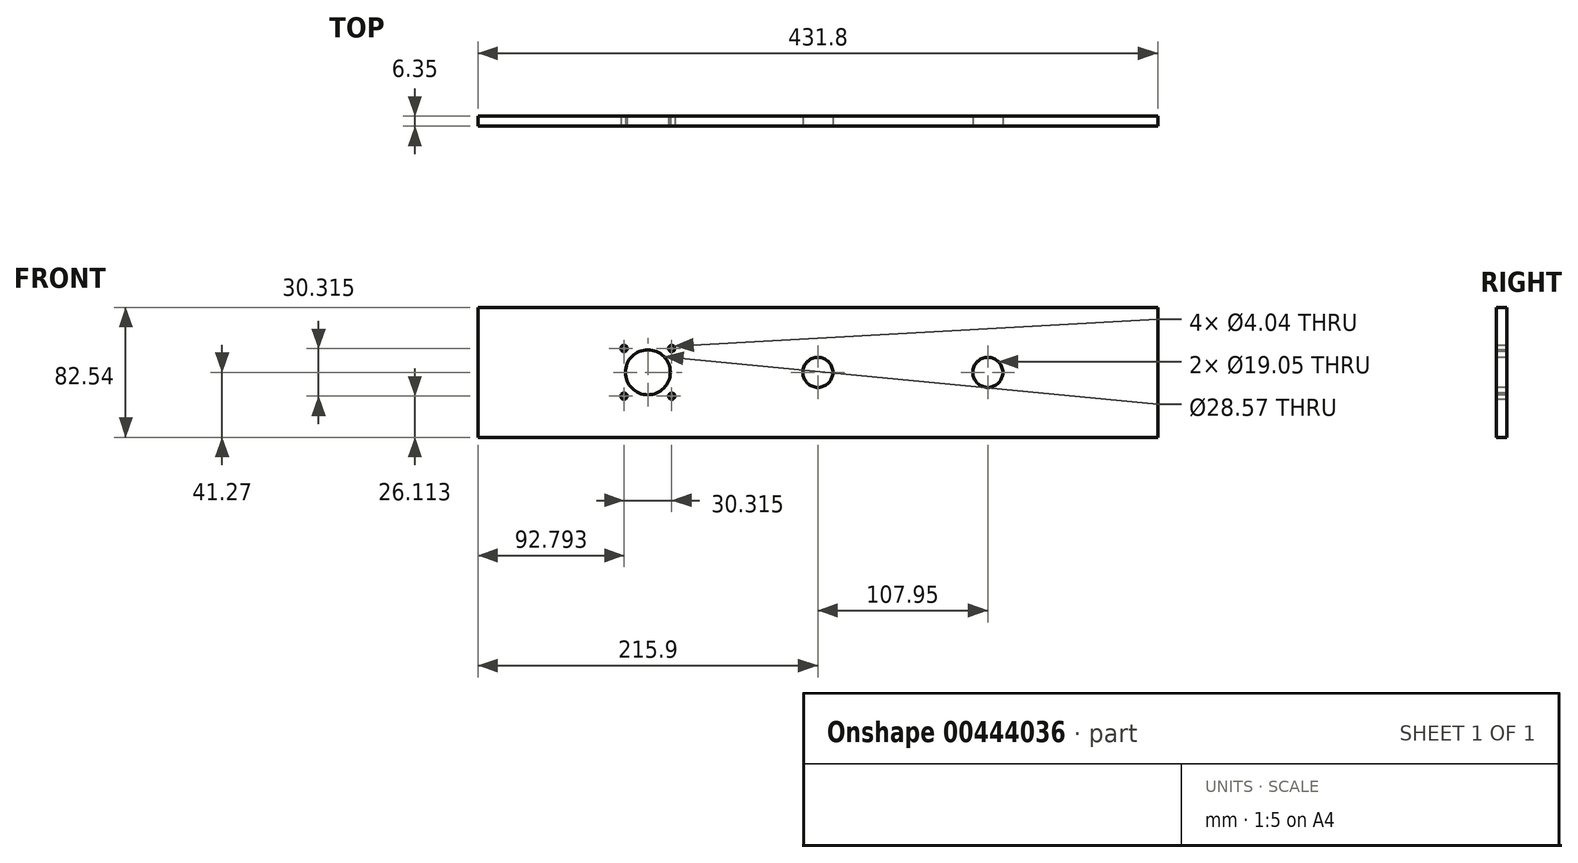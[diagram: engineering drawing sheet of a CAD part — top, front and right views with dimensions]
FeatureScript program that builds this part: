
annotation { "Feature Type Name" : "Feature", "Feature Type Description" : "" }
export const myFeature = defineFeature(function(context is Context, id is Id, definition is map)
    precondition{}
    {
        {
            var Q0;
            Q0=qCreatedBy(makeId("Front.planeOp"),FACE);
            var sketch = newSketch(context, id + "F0", { "sketchPlane" : qUnion([Q0])});
            skLineSegment(sketch, "E0.bottom", {"start": v(215.9, 41.28) * mm, "end": v(-215.9, 41.28) * mm});
            skLineSegment(sketch, "E0.top", {"start": v(215.9, -41.28) * mm, "end": v(-215.9, -41.28) * mm});
            skLineSegment(sketch, "E0.left", {"start": v(215.9, 41.28) * mm, "end": v(215.9, -41.28) * mm});
            skLineSegment(sketch, "E0.right", {"start": v(-215.9, 41.28) * mm, "end": v(-215.9, -41.28) * mm});
            skPoint(sketch, "E0.middle", {"position": v(0, 0) * mm});
            skSolve(sketch);
        }
        {
            var Q0;
            Q0=makeQuery(id+"F0.imprint","IMPRINT",FACE,{"disambiguationData":[TD([[makeQuery(id+"F0.imprint","IMPRINT",EDGE,{"derivedFrom":sQuery(id+"F0.wireOp",EDGE,"E0.bottom")}),1.0]])]});
            extrude(context, id + "F1", {"entities" : qUnion([Q0]), "depth" : 6.35 * mm});
        }
        {
            var Q0;
            Q0=makeQuery(id+"F1.opExtrude","CAP_FACE",FACE,{"disambiguationData":[OSD([sQuery(id+"F0.wireOp",EDGE,"E0.bottom"),sQuery(id+"F0.wireOp",EDGE,"E0.top"),sQuery(id+"F0.wireOp",EDGE,"E0.left"),sQuery(id+"F0.wireOp",EDGE,"E0.right")])],"isStart":false});
            var sketch = newSketch(context, id + "F2", { "sketchPlane" : qUnion([Q0])});
            skLineSegment(sketch, "E1", {"start": v(-215.9, 0) * mm, "end": v(215.9, 0) * mm});
            skCircle(sketch, "E2", {"center": v(107.95, 0) * mm, "radius": 9.53 * mm});
            skCircle(sketch, "E3", {"center": v(0, 0) * mm, "radius": 9.53 * mm});
            skCircle(sketch, "E4", {"center": v(-107.95, 0) * mm, "radius": 14.29 * mm});
            skSolve(sketch);
        }
        {
            var Q0;
            Q0 = qSketchRegion(id + "F2", true);
            var Q1;
            Q1=makeQuery(id+"F1.opExtrude","CAP_FACE",FACE,{"disambiguationData":[OSD([sQuery(id+"F0.wireOp",EDGE,"E0.bottom"),sQuery(id+"F0.wireOp",EDGE,"E0.top"),sQuery(id+"F0.wireOp",EDGE,"E0.left"),sQuery(id+"F0.wireOp",EDGE,"E0.right")])],"isStart":true});
            extrude(context, id + "F3", {"entities" : qUnion([Q0]), "operationType" : NewBodyOperationType.REMOVE, "endBound" : BoundingType.UP_TO_SURFACE, "oppositeDirection" : true, "endBoundEntityFace" : qUnion([Q1]), "depth" : 25.4 * mm});
        }
        {
            var Q0;
            Q0=makeQuery(id+"F1.opExtrude","CAP_FACE",FACE,{"disambiguationData":[OSD([sQuery(id+"F0.wireOp",EDGE,"E0.bottom"),sQuery(id+"F0.wireOp",EDGE,"E0.top"),sQuery(id+"F0.wireOp",EDGE,"E0.left"),sQuery(id+"F0.wireOp",EDGE,"E0.right")])],"isStart":false});
            var sketch = newSketch(context, id + "F4", { "sketchPlane" : qUnion([Q0])});
            skLineSegment(sketch, "E5", {"start": v(-107.95, 0) * mm, "end": v(-107.95, 15.16) * mm});
            skLineSegment(sketch, "E6", {"start": v(-107.95, 15.16) * mm, "end": v(-92.8, 15.16) * mm});
            skLineSegment(sketch, "E7", {"start": v(-92.8, 15.16) * mm, "end": v(-92.8, -15.16) * mm});
            skLineSegment(sketch, "E8", {"start": v(-92.8, -15.16) * mm, "end": v(-123.1, -15.16) * mm});
            skLineSegment(sketch, "E9", {"start": v(-123.1, -15.16) * mm, "end": v(-123.1, 15.16) * mm});
            skLineSegment(sketch, "E10", {"start": v(-123.1, 15.16) * mm, "end": v(-107.95, 15.16) * mm});
            skCircle(sketch, "E11", {"center": v(-92.8, 15.16) * mm, "radius": 2.02 * mm});
            skCircle(sketch, "E12", {"center": v(-92.8, -15.16) * mm, "radius": 2.02 * mm});
            skCircle(sketch, "E13", {"center": v(-123.1, -15.16) * mm, "radius": 2.02 * mm});
            skCircle(sketch, "E14", {"center": v(-123.1, 15.16) * mm, "radius": 2.02 * mm});
            skSolve(sketch);
        }
        {
            var Q0;
            {var subQ0=sQuery(id+"F4.wireOp",EDGE,"E9");var subQ1=sQuery(id+"F4.wireOp",EDGE,"E8");var subQ2=makeQuery(id+"F4.imprint","INTERSECT",VERTEX,{"derivedFrom":[subQ1,subQ0]});Q0=makeQuery(id+"F4.imprint","IMPRINT",FACE,{"disambiguationData":[TD([[makeQuery(id+"F4.imprint","IMPRINT",EDGE,{"disambiguationData":[TD([[subQ2,1.0]])],"derivedFrom":subQ1}),1.0]])]});}
            var Q1;
            {var subQ0=sQuery(id+"F4.wireOp",EDGE,"E9");var subQ1=sQuery(id+"F4.wireOp",EDGE,"E8");var subQ2=makeQuery(id+"F4.imprint","INTERSECT",VERTEX,{"derivedFrom":[subQ1,subQ0]});Q1=makeQuery(id+"F4.imprint","IMPRINT",FACE,{"disambiguationData":[TD([[makeQuery(id+"F4.imprint","IMPRINT",EDGE,{"disambiguationData":[TD([[subQ2,1.0]])],"derivedFrom":subQ1}),-1.0]])]});}
            var Q2;
            {var subQ0=sQuery(id+"F4.wireOp",EDGE,"E8");var subQ1=sQuery(id+"F4.wireOp",EDGE,"E7");var subQ2=makeQuery(id+"F4.imprint","INTERSECT",VERTEX,{"derivedFrom":[subQ1,subQ0]});Q2=makeQuery(id+"F4.imprint","IMPRINT",FACE,{"disambiguationData":[TD([[makeQuery(id+"F4.imprint","IMPRINT",EDGE,{"disambiguationData":[TD([[subQ2,1.0]])],"derivedFrom":subQ1}),1.0]])]});}
            var Q3;
            {var subQ0=sQuery(id+"F4.wireOp",EDGE,"E8");var subQ1=sQuery(id+"F4.wireOp",EDGE,"E7");var subQ2=makeQuery(id+"F4.imprint","INTERSECT",VERTEX,{"derivedFrom":[subQ1,subQ0]});Q3=makeQuery(id+"F4.imprint","IMPRINT",FACE,{"disambiguationData":[TD([[makeQuery(id+"F4.imprint","IMPRINT",EDGE,{"disambiguationData":[TD([[subQ2,1.0]])],"derivedFrom":subQ1}),-1.0]])]});}
            var Q4;
            {var subQ0=sQuery(id+"F4.wireOp",EDGE,"E7");var subQ1=sQuery(id+"F4.wireOp",EDGE,"E6");var subQ2=makeQuery(id+"F4.imprint","INTERSECT",VERTEX,{"derivedFrom":[subQ1,subQ0]});Q4=makeQuery(id+"F4.imprint","IMPRINT",FACE,{"disambiguationData":[TD([[makeQuery(id+"F4.imprint","IMPRINT",EDGE,{"disambiguationData":[TD([[subQ2,1.0]])],"derivedFrom":subQ1}),-1.0]])]});}
            var Q5;
            {var subQ0=sQuery(id+"F4.wireOp",EDGE,"E7");var subQ1=sQuery(id+"F4.wireOp",EDGE,"E6");var subQ2=makeQuery(id+"F4.imprint","INTERSECT",VERTEX,{"derivedFrom":[subQ1,subQ0]});Q5=makeQuery(id+"F4.imprint","IMPRINT",FACE,{"disambiguationData":[TD([[makeQuery(id+"F4.imprint","IMPRINT",EDGE,{"disambiguationData":[TD([[subQ2,1.0]])],"derivedFrom":subQ1}),1.0]])]});}
            var Q6;
            {var subQ0=sQuery(id+"F4.wireOp",EDGE,"E10");var subQ1=sQuery(id+"F4.wireOp",EDGE,"E9");var subQ2=makeQuery(id+"F4.imprint","INTERSECT",VERTEX,{"derivedFrom":[subQ1,subQ0]});Q6=makeQuery(id+"F4.imprint","IMPRINT",FACE,{"disambiguationData":[TD([[makeQuery(id+"F4.imprint","IMPRINT",EDGE,{"disambiguationData":[TD([[subQ2,1.0]])],"derivedFrom":subQ1}),-1.0]])]});}
            var Q7;
            {var subQ0=sQuery(id+"F4.wireOp",EDGE,"E10");var subQ1=sQuery(id+"F4.wireOp",EDGE,"E9");var subQ2=makeQuery(id+"F4.imprint","INTERSECT",VERTEX,{"derivedFrom":[subQ1,subQ0]});Q7=makeQuery(id+"F4.imprint","IMPRINT",FACE,{"disambiguationData":[TD([[makeQuery(id+"F4.imprint","IMPRINT",EDGE,{"disambiguationData":[TD([[subQ2,1.0]])],"derivedFrom":subQ1}),1.0]])]});}
            var Q8;
            Q8=makeQuery(id+"F1.opExtrude","CAP_FACE",FACE,{"disambiguationData":[OSD([sQuery(id+"F0.wireOp",EDGE,"E0.bottom"),sQuery(id+"F0.wireOp",EDGE,"E0.top"),sQuery(id+"F0.wireOp",EDGE,"E0.left"),sQuery(id+"F0.wireOp",EDGE,"E0.right")])],"isStart":true});
            extrude(context, id + "F5", {"entities" : qUnion([Q0, Q1, Q2, Q3, Q4, Q5, Q6, Q7]), "operationType" : NewBodyOperationType.REMOVE, "endBound" : BoundingType.UP_TO_SURFACE, "oppositeDirection" : true, "endBoundEntityFace" : qUnion([Q8]), "depth" : 25.4 * mm});
        }
    });
